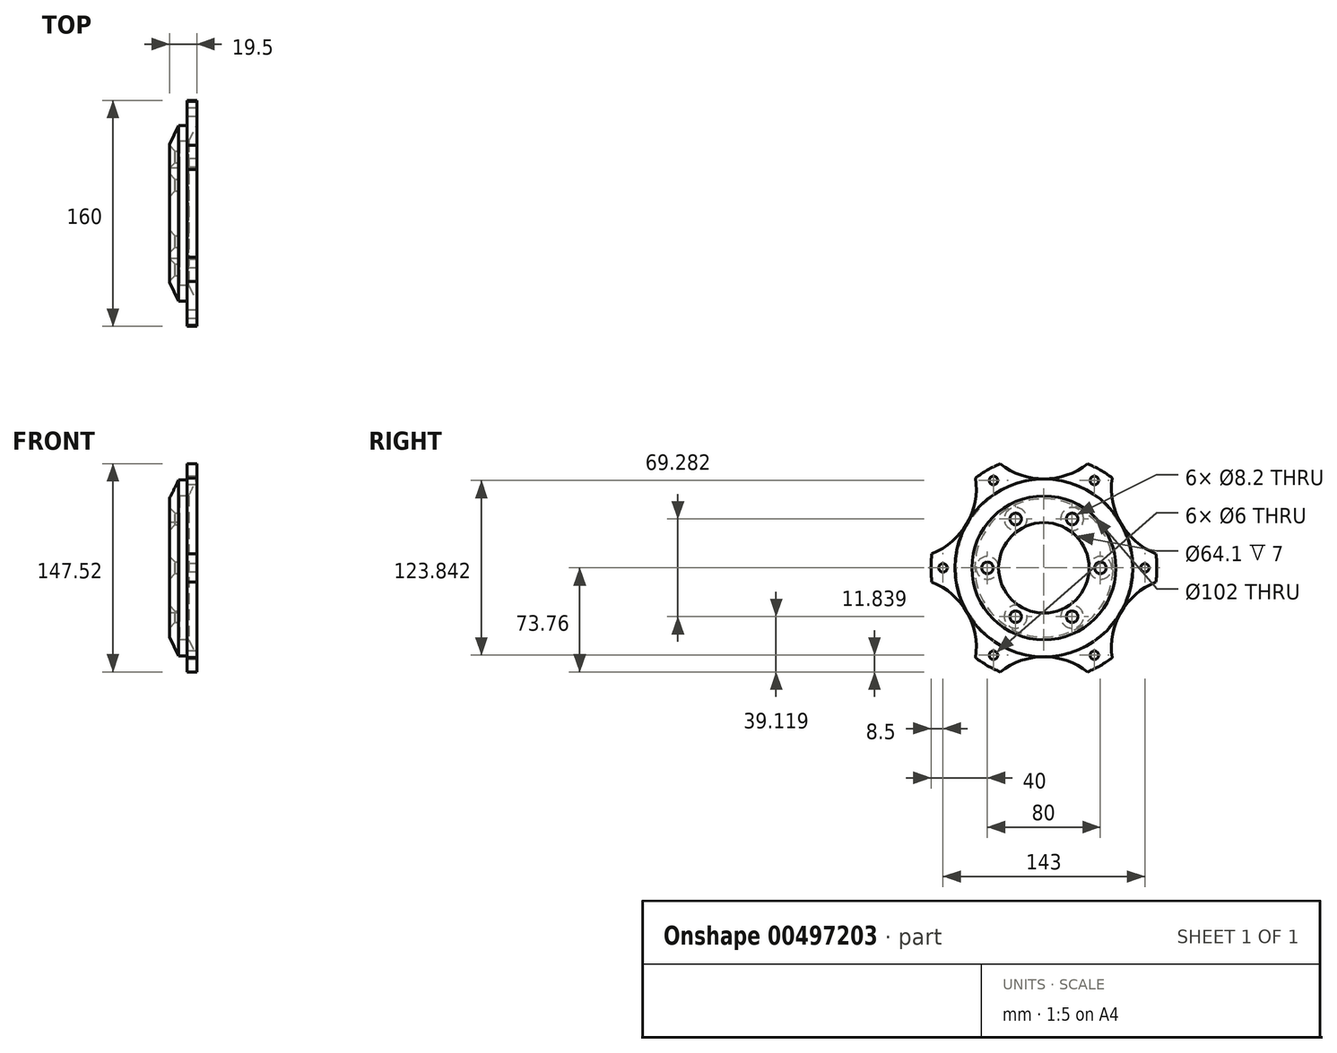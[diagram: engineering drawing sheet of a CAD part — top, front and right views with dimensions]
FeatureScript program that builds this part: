
annotation { "Feature Type Name" : "Feature", "Feature Type Description" : "" }
export const myFeature = defineFeature(function(context is Context, id is Id, definition is map)
    precondition{}
    {
        {
            var Q0;
            Q0=qCreatedBy(makeId("Top.planeOp"),FACE);
            var sketch = newSketch(context, id + "F0", { "sketchPlane" : qUnion([Q0])});
            skLineSegment(sketch, "E0", {"start": v(-7, 32.05) * mm, "end": v(0, 32.05) * mm});
            skLineSegment(sketch, "E1", {"start": v(0, 32.05) * mm, "end": v(0, 51) * mm});
            skLineSegment(sketch, "E2", {"start": v(12.5, 80) * mm, "end": v(5.5, 80) * mm});
            skLineSegment(sketch, "E3", {"start": v(5.5, 80) * mm, "end": v(5.5, 62.3) * mm});
            skLineSegment(sketch, "E4", {"start": v(5.5, 62.3) * mm, "end": v(-0.5, 62.3) * mm});
            skLineSegment(sketch, "E5", {"start": v(-0.5, 62.3) * mm, "end": v(-7, 49) * mm});
            skLineSegment(sketch, "E6", {"start": v(-7, 49) * mm, "end": v(-7, 32.05) * mm});
            skLineSegment(sketch, "E7", {"start": v(-7, 0) * mm, "end": v(0, 0) * mm, "construction": true});
            skLineSegment(sketch, "E8", {"start": v(0, 51) * mm, "end": v(6.66, 51) * mm});
            skLineSegment(sketch, "E9", {"start": v(12.5, 62.96) * mm, "end": v(12.5, 80) * mm});
            skLineSegment(sketch, "E10", {"start": v(6.66, 51) * mm, "end": v(12.5, 62.96) * mm});
            skSolve(sketch);
        }
        {
            var Q0;
            Q0=makeQuery(id+"F0.imprint","IMPRINT",FACE,{"disambiguationData":[TD([[makeQuery(id+"F0.imprint","IMPRINT",EDGE,{"derivedFrom":sQuery(id+"F0.wireOp",EDGE,"6ztelrAd-LknY-4zA2-EE4v-fHWb3Nsfnenm")}),1.0]])]});
            var Q1;
            Q1=makeQuery(id+"F0.imprint","IMPRINT",FACE,{"disambiguationData":[TD([[makeQuery(id+"F0.imprint","IMPRINT",EDGE,{"derivedFrom":sQuery(id+"F0.wireOp",EDGE,"E0")}),1.0]])]});
            var Q2;
            Q2=sQuery(id+"F0.wireOp",EDGE,"E7");
            revolve(context, id + "F1", {"entities" : qUnion([Q0, Q1]), "axis" : qUnion([Q2]), "revolveType" : RevolveType.FULL});
        }
        {
            var Q0;
            Q0=qCreatedBy(makeId("Right.planeOp"),FACE);
            var sketch = newSketch(context, id + "F2", { "sketchPlane" : qUnion([Q0])});
            skCircle(sketch, "E11", {"center": v(-40, 0) * mm, "radius": 4.1 * mm});
            skCircle(sketch, "E12.1.0", {"center": v(-20, -34.64) * mm, "radius": 4.1 * mm});
            skCircle(sketch, "E12.2.0", {"center": v(20, -34.64) * mm, "radius": 4.1 * mm});
            skCircle(sketch, "E12.3.0", {"center": v(40, 0) * mm, "radius": 4.1 * mm});
            skCircle(sketch, "E12.4.0", {"center": v(20, 34.64) * mm, "radius": 4.1 * mm});
            skPoint(sketch, "E12.center", {"position": v(0, 0) * mm});
            skCircle(sketch, "E13.1.5.0", {"center": v(-20, 34.64) * mm, "radius": 4.1 * mm});
            skSolve(sketch);
        }
        {
            var Q0;
            Q0 = qSketchRegion(id + "F2", true);
            extrude(context, id + "F3", {"entities" : qUnion([Q0]), "operationType" : NewBodyOperationType.REMOVE, "endBound" : BoundingType.SYMMETRIC, "oppositeDirection" : true, "depth" : 100 * mm});
        }
        {
            var Q0;
            Q0=makeQuery(id+"F1.opRevolve","SWEPT_FACE",FACE,{"disambiguationData":[OSD([sQuery(id+"F0.wireOp",EDGE,"E3")])]});
            var sketch = newSketch(context, id + "F4", { "sketchPlane" : qUnion([Q0])});
            skCircle(sketch, "E14", {"center": v(35.75, 61.92) * mm, "radius": 3 * mm});
            skLineSegment(sketch, "E15", {"start": v(35.75, 61.92) * mm, "end": v(0, 0) * mm, "construction": true});
            skPoint(sketch, "E16.center", {"position": v(0, 0) * mm});
            skCircle(sketch, "E17.1.0", {"center": v(-35.75, 61.92) * mm, "radius": 3 * mm});
            skCircle(sketch, "E17.2.0", {"center": v(-71.5, 0) * mm, "radius": 3 * mm});
            skCircle(sketch, "E18.1.3.0", {"center": v(-35.75, -61.92) * mm, "radius": 3 * mm});
            skCircle(sketch, "E18.1.4.0", {"center": v(35.75, -61.92) * mm, "radius": 3 * mm});
            skCircle(sketch, "E18.1.5.0", {"center": v(71.5, 0) * mm, "radius": 3 * mm});
            skSolve(sketch);
        }
        {
            var Q0;
            Q0 = qSketchRegion(id + "F4", true);
            extrude(context, id + "F5", {"entities" : qUnion([Q0]), "operationType" : NewBodyOperationType.REMOVE, "endBound" : BoundingType.SYMMETRIC, "oppositeDirection" : true, "depth" : 100 * mm});
        }
        {
            var Q0;
            Q0=makeQuery(id+"F3.boolean.opBoolean","INTERSECT",EDGE,{"derivedFrom":[makeQuery(id+"F1.opRevolve","SWEPT_FACE",FACE,{"disambiguationData":[OSD([sQuery(id+"F0.wireOp",EDGE,"E6")])]}),makeQuery(id+"F3.opExtrude","SWEPT_FACE",FACE,{"disambiguationData":[OSD([sQuery(id+"F2.wireOp",EDGE,"E12.4.0")])]})]});
            var Q1;
            Q1=makeQuery(id+"F3.boolean.opBoolean","INTERSECT",EDGE,{"derivedFrom":[makeQuery(id+"F1.opRevolve","SWEPT_FACE",FACE,{"disambiguationData":[OSD([sQuery(id+"F0.wireOp",EDGE,"E6")])]}),makeQuery(id+"F3.opExtrude","SWEPT_FACE",FACE,{"disambiguationData":[OSD([sQuery(id+"F2.wireOp",EDGE,"E13.1.5.0")])]})]});
            var Q2;
            Q2=makeQuery(id+"F3.boolean.opBoolean","INTERSECT",EDGE,{"derivedFrom":[makeQuery(id+"F1.opRevolve","SWEPT_FACE",FACE,{"disambiguationData":[OSD([sQuery(id+"F0.wireOp",EDGE,"E6")])]}),makeQuery(id+"F3.opExtrude","SWEPT_FACE",FACE,{"disambiguationData":[OSD([sQuery(id+"F2.wireOp",EDGE,"E11")])]})]});
            var Q3;
            Q3=makeQuery(id+"F3.boolean.opBoolean","INTERSECT",EDGE,{"derivedFrom":[makeQuery(id+"F1.opRevolve","SWEPT_FACE",FACE,{"disambiguationData":[OSD([sQuery(id+"F0.wireOp",EDGE,"E6")])]}),makeQuery(id+"F3.opExtrude","SWEPT_FACE",FACE,{"disambiguationData":[OSD([sQuery(id+"F2.wireOp",EDGE,"E12.1.0")])]})]});
            var Q4;
            Q4=makeQuery(id+"F3.boolean.opBoolean","INTERSECT",EDGE,{"derivedFrom":[makeQuery(id+"F1.opRevolve","SWEPT_FACE",FACE,{"disambiguationData":[OSD([sQuery(id+"F0.wireOp",EDGE,"E6")])]}),makeQuery(id+"F3.opExtrude","SWEPT_FACE",FACE,{"disambiguationData":[OSD([sQuery(id+"F2.wireOp",EDGE,"E12.2.0")])]})]});
            var Q5;
            Q5=makeQuery(id+"F3.boolean.opBoolean","INTERSECT",EDGE,{"derivedFrom":[makeQuery(id+"F1.opRevolve","SWEPT_FACE",FACE,{"disambiguationData":[OSD([sQuery(id+"F0.wireOp",EDGE,"E6")])]}),makeQuery(id+"F3.opExtrude","SWEPT_FACE",FACE,{"disambiguationData":[OSD([sQuery(id+"F2.wireOp",EDGE,"E12.3.0")])]})]});
            chamfer(context, id + "F6", {"entities" : qUnion([Q0, Q1, Q2, Q3, Q4, Q5]), "width" : 4 * mm, "tangentPropagation" : true});
        }
        {
            var Q0;
            Q0=makeQuery(id+"F1.opRevolve","SWEPT_EDGE",EDGE,{"disambiguationData":[OSD([sQuery(id+"F0.wireOp",EDGE,"E1"),sQuery(id+"F0.wireOp",EDGE,"E8")])]});
            fillet(context, id + "F7", {"entities" : qUnion([Q0]), "radius" : 1 * mm, "tangentPropagation" : true, "allowEdgeOverflow" : false});
        }
        {
            var Q0;
            Q0=makeQuery(id+"F1.opRevolve","SWEPT_FACE",FACE,{"disambiguationData":[OSD([sQuery(id+"F0.wireOp",EDGE,"E3")])]});
            var sketch = newSketch(context, id + "F8", { "sketchPlane" : qUnion([Q0])});
            skCircle(sketch, "E19", {"center": v(0, 113) * mm, "radius": 50 * mm});
            skCircle(sketch, "E20.1.0", {"center": v(-97.86, 56.5) * mm, "radius": 50 * mm});
            skCircle(sketch, "E20.2.0", {"center": v(-97.86, -56.5) * mm, "radius": 50 * mm});
            skCircle(sketch, "E20.3.0", {"center": v(0, -113) * mm, "radius": 50 * mm});
            skCircle(sketch, "E20.4.0", {"center": v(97.86, -56.5) * mm, "radius": 50 * mm});
            skCircle(sketch, "E20.5.0", {"center": v(97.86, 56.5) * mm, "radius": 50 * mm});
            skPoint(sketch, "E20.center", {"position": v(0, 0) * mm});
            skSolve(sketch);
        }
        {
            var Q0;
            Q0 = qSketchRegion(id + "F8", true);
            extrude(context, id + "F9", {"entities" : qUnion([Q0]), "operationType" : NewBodyOperationType.REMOVE, "endBound" : BoundingType.SYMMETRIC, "oppositeDirection" : true, "depth" : 100 * mm});
        }
    });
